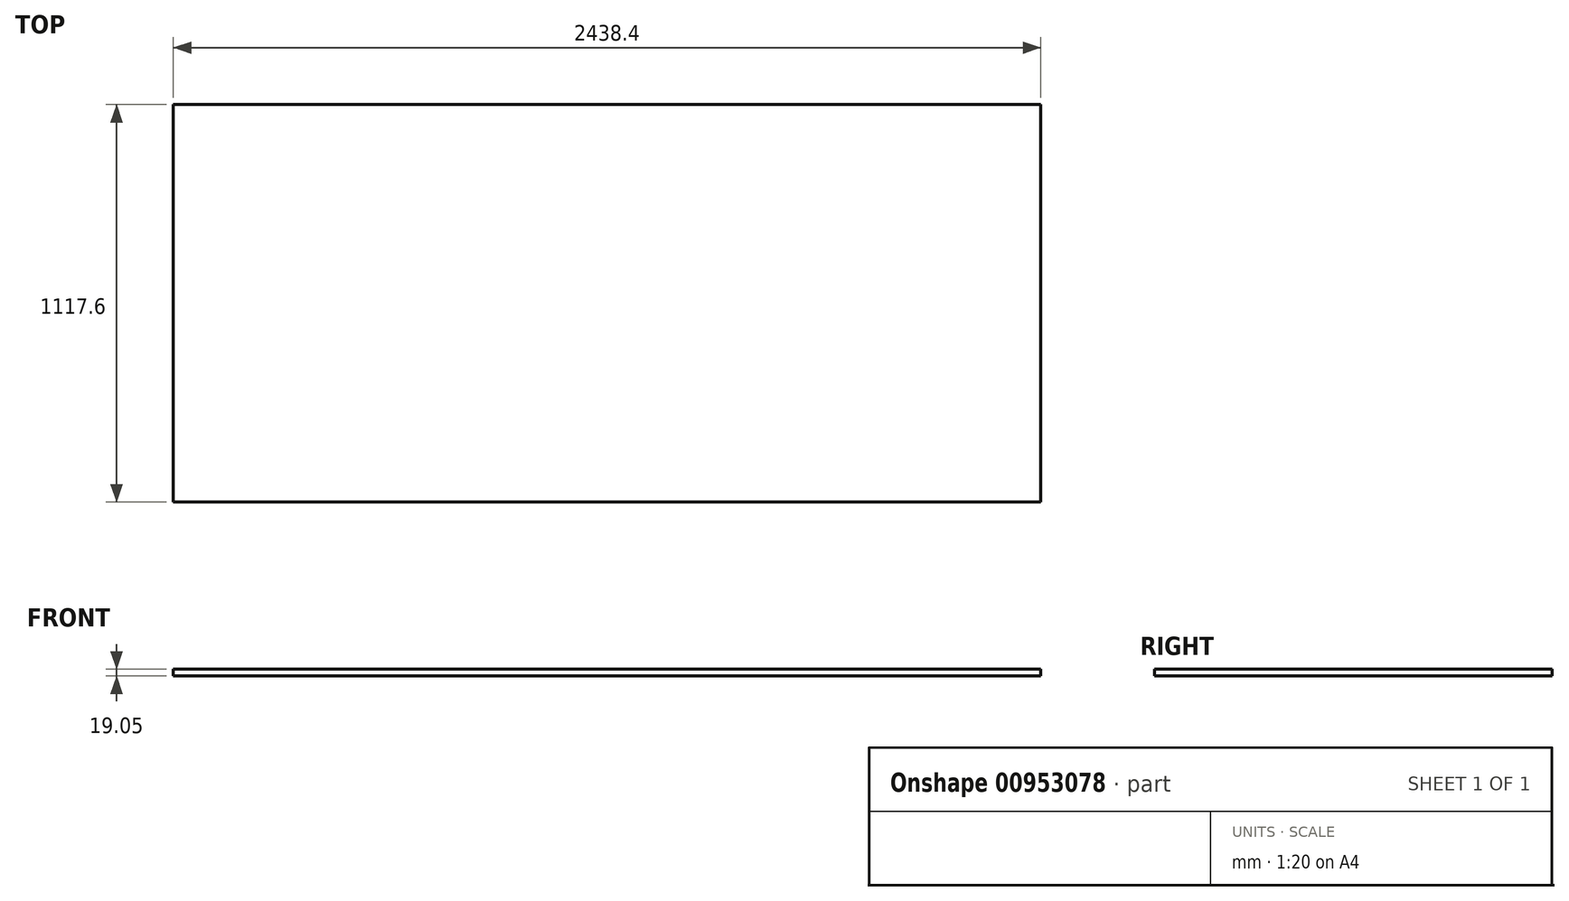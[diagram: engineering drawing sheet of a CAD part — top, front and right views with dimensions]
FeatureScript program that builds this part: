
annotation { "Feature Type Name" : "Feature", "Feature Type Description" : "" }
export const myFeature = defineFeature(function(context is Context, id is Id, definition is map)
    precondition{}
    {
        {
            var Q0;
            Q0=qCreatedBy(makeId("Top.planeOp"),FACE);
            var sketch = newSketch(context, id + "F0", { "sketchPlane" : qUnion([Q0])});
            skLineSegment(sketch, "E0", {"start": v(0, 0) * mm, "end": v(-2438.4, 0) * mm});
            skLineSegment(sketch, "E1", {"start": v(-2438.4, 0) * mm, "end": v(-2438.4, 1117.6) * mm});
            skLineSegment(sketch, "E2", {"start": v(-2438.4, 1117.6) * mm, "end": v(0, 1117.6) * mm});
            skLineSegment(sketch, "E3", {"start": v(0, 1117.6) * mm, "end": v(0, 0) * mm});
            skSolve(sketch);
        }
        {
            var Q0;
            Q0 = qSketchRegion(id + "F0", true);
            extrude(context, id + "F1", {"entities" : qUnion([Q0]), "depth" : 19.05 * mm, "offsetDistance" : 25.4 * mm});
        }
    });
